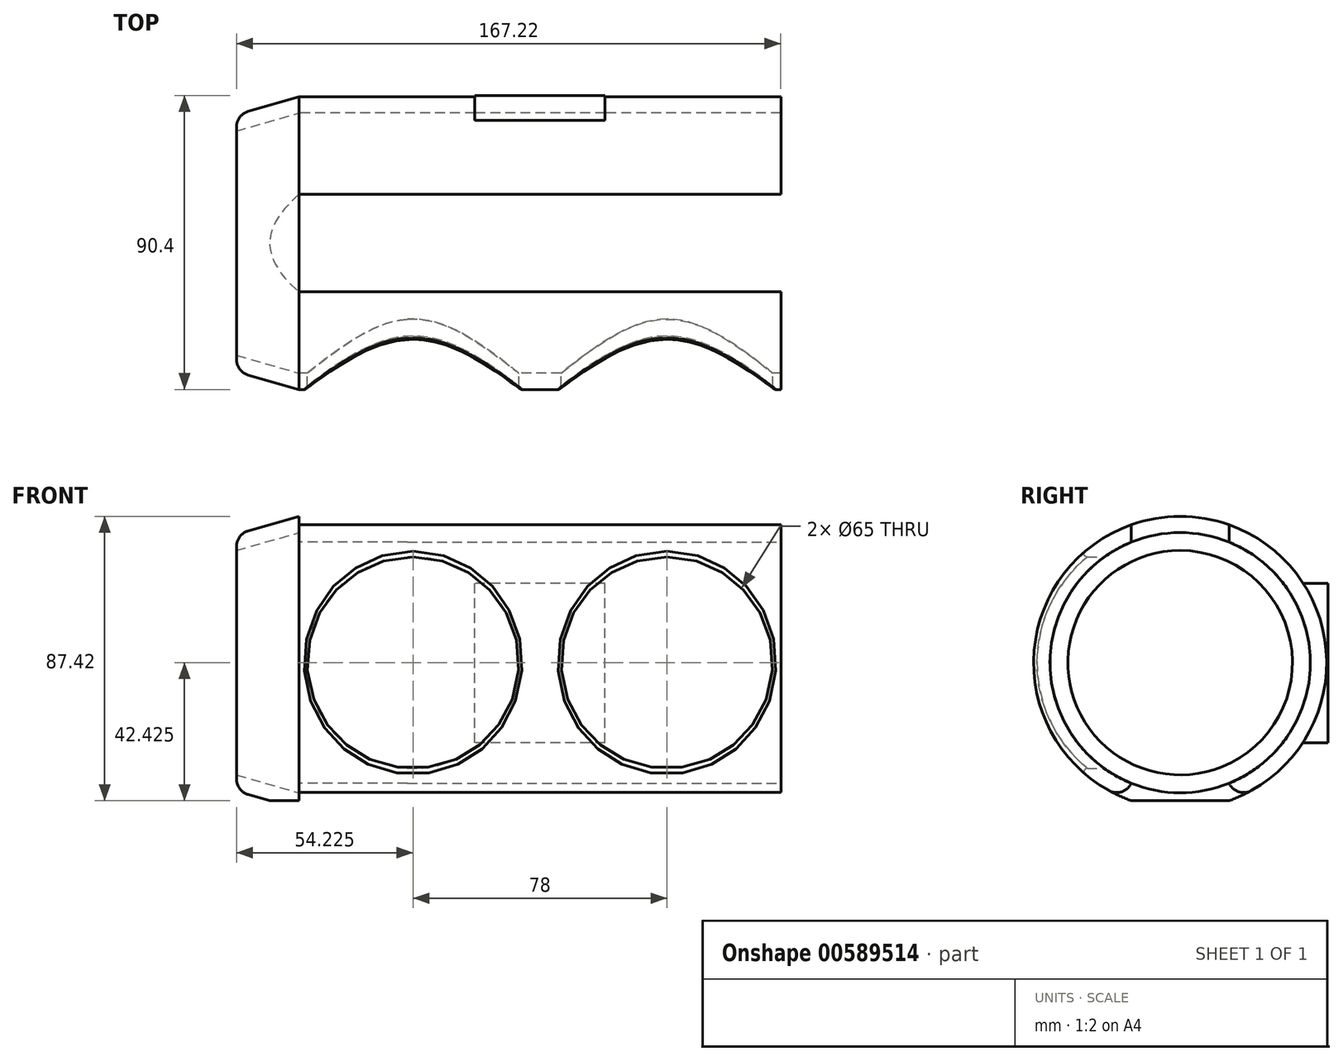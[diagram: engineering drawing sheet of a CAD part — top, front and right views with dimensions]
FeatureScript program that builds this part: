
annotation { "Feature Type Name" : "Feature", "Feature Type Description" : "" }
export const myFeature = defineFeature(function(context is Context, id is Id, definition is map)
    precondition{}
    {
        {
            var Q0;
            Q0=qCreatedBy(makeId("Front.planeOp"),FACE);
            var sketch = newSketch(context, id + "F0", { "sketchPlane" : qUnion([Q0])});
            skLineSegment(sketch, "E0.left", {"start": v(-52.48, 41.98) * mm, "end": v(-52.48, 7.48) * mm});
            skLineSegment(sketch, "E0.right", {"start": v(-33.26, 47.48) * mm, "end": v(-33.26, 7.48) * mm});
            skLineSegment(sketch, "E1", {"start": v(-52.48, 41.98) * mm, "end": v(-33.26, 47.48) * mm});
            skLineSegment(sketch, "E2", {"start": v(-52.48, 7.48) * mm, "end": v(-33.26, 7.48) * mm});
            skLineSegment(sketch, "E3", {"start": v(-33.26, 47.48) * mm, "end": v(-33.26, 52.48) * mm});
            skLineSegment(sketch, "E4", {"start": v(-52.48, 41.98) * mm, "end": v(-52.48, 46.98) * mm});
            skLineSegment(sketch, "E5", {"start": v(-52.48, 46.98) * mm, "end": v(-33.26, 52.48) * mm});
            skLineSegment(sketch, "E6.MirrorCS", {"start": v(-33.26, -32.52) * mm, "end": v(-33.26, 7.48) * mm});
            skLineSegment(sketch, "E7.MirrorCS", {"start": v(-52.48, -27.02) * mm, "end": v(-52.48, 7.48) * mm});
            skLineSegment(sketch, "E8.MirrorCS", {"start": v(-52.48, -27.02) * mm, "end": v(-33.26, -32.52) * mm});
            skLineSegment(sketch, "E9.MirrorCS", {"start": v(-52.48, -32.02) * mm, "end": v(-33.26, -37.52) * mm});
            skLineSegment(sketch, "E10.MirrorCS", {"start": v(-52.48, -27.02) * mm, "end": v(-52.48, -32.02) * mm});
            skLineSegment(sketch, "E11.MirrorCS", {"start": v(-33.26, -32.52) * mm, "end": v(-33.26, -37.52) * mm});
            skLineSegment(sketch, "E12", {"start": v(-33.26, 47.48) * mm, "end": v(114.74, 47.48) * mm});
            skLineSegment(sketch, "E13", {"start": v(40.74, 47.48) * mm, "end": v(40.74, -32.52) * mm});
            skLineSegment(sketch, "E14.MirrorCS", {"start": v(114.74, -32.52) * mm, "end": v(114.74, 7.48) * mm});
            skLineSegment(sketch, "E15.MirrorCS", {"start": v(114.74, 47.48) * mm, "end": v(114.74, 7.48) * mm});
            skLineSegment(sketch, "E16.MirrorCS", {"start": v(114.74, -32.52) * mm, "end": v(114.74, -37.52) * mm});
            skLineSegment(sketch, "E17.MirrorCS", {"start": v(114.74, 47.48) * mm, "end": v(114.74, 52.48) * mm});
            skLineSegment(sketch, "E18.MirrorCS", {"start": v(114.74, 47.48) * mm, "end": v(-33.26, 47.48) * mm});
            skLineSegment(sketch, "E19.MirrorCS", {"start": v(-33.26, -32.52) * mm, "end": v(114.74, -32.52) * mm});
            skLineSegment(sketch, "E20", {"start": v(-33.26, 52.48) * mm, "end": v(114.74, 52.48) * mm});
            skLineSegment(sketch, "E21", {"start": v(-33.26, -37.52) * mm, "end": v(114.74, -37.52) * mm});
            skSolve(sketch);
        }
        {
            var Q0;
            Q0=makeQuery(id+"F0.imprint","IMPRINT",FACE,{"disambiguationData":[TD([[makeQuery(id+"F0.imprint","IMPRINT",EDGE,{"derivedFrom":sQuery(id+"F0.wireOp",EDGE,"E1")}),1.0]])]});
            var Q1;
            Q1=makeQuery(id+"F0.imprint","IMPRINT",FACE,{"disambiguationData":[TD([[makeQuery(id+"F0.imprint","IMPRINT",EDGE,{"derivedFrom":sQuery(id+"F0.wireOp",EDGE,"c2bfdc4a-e5b6-459e-925a-0be5c92ff4e80.MirrorCS")}),-1.0]])]});
            var Q2;
            {var subQ1=sQuery(id+"F0.wireOp",EDGE,"E3");Q2=makeQuery(id+"F0.imprint","IMPRINT",FACE,{"disambiguationData":[TD([[makeQuery(id+"F0.imprint","IMPRINT",EDGE,{"derivedFrom":subQ1}),-1.0]])]});}
            var Q3;
            Q3=sQuery(id+"F0.wireOp",EDGE,"E2");
            revolve(context, id + "F1", {"entities" : qUnion([Q0, Q1, Q2]), "axis" : qUnion([Q3]), "revolveType" : RevolveType.FULL});
        }
        {
            var Q0;
            Q0=qCreatedBy(makeId("Top.planeOp"),FACE);
            var sketch = newSketch(context, id + "F2", { "sketchPlane" : qUnion([Q0])});
            skLineSegment(sketch, "E22", {"start": v(-33.26, 0) * mm, "end": v(114.74, 0) * mm});
            skLineSegment(sketch, "E23.bottom", {"start": v(114.74, -15) * mm, "end": v(-33.26, -15) * mm});
            skLineSegment(sketch, "E23.top", {"start": v(114.74, 15) * mm, "end": v(-33.26, 15) * mm});
            skLineSegment(sketch, "E23.left", {"start": v(114.74, -15) * mm, "end": v(114.74, 15) * mm});
            skLineSegment(sketch, "E23.right", {"start": v(-33.26, -15) * mm, "end": v(-33.26, 15) * mm});
            skPoint(sketch, "E23.middle", {"position": v(40.74, 0) * mm});
            skSolve(sketch);
        }
        {
            var Q0;
            Q0 = qSketchRegion(id + "F2", true);
            extrude(context, id + "F3", {"entities" : qUnion([Q0]), "operationType" : NewBodyOperationType.REMOVE, "endBound" : BoundingType.SYMMETRIC, "depth" : 116.8 * mm, "offsetDistance" : 25 * mm});
        }
        {
            var Q0;
            Q0=qCreatedBy(makeId("Front.planeOp"),FACE);
            var sketch = newSketch(context, id + "F4", { "sketchPlane" : qUnion([Q0])});
            skCircle(sketch, "E24", {"center": v(1.74, 7.48) * mm, "radius": 32.5 * mm});
            skCircle(sketch, "E25", {"center": v(79.74, 7.48) * mm, "radius": 32.5 * mm});
            skSolve(sketch);
        }
        {
            var Q0;
            Q0=qCreatedBy(makeId("Front.planeOp"),FACE);
            var sketch = newSketch(context, id + "F5", { "sketchPlane" : qUnion([Q0])});
            skLineSegment(sketch, "E26.bottom", {"start": v(-49.57, -47.9) * mm, "end": v(133.44, -47.9) * mm});
            skLineSegment(sketch, "E26.top", {"start": v(-49.57, -34.94) * mm, "end": v(133.44, -34.94) * mm});
            skLineSegment(sketch, "E26.left", {"start": v(-49.57, -47.9) * mm, "end": v(-49.57, -34.94) * mm});
            skLineSegment(sketch, "E26.right", {"start": v(133.44, -47.9) * mm, "end": v(133.44, -34.94) * mm});
            skSolve(sketch);
        }
        {
            var Q0;
            Q0 = qSketchRegion(id + "F5", true);
            extrude(context, id + "F6", {"entities" : qUnion([Q0]), "operationType" : NewBodyOperationType.REMOVE, "endBound" : BoundingType.SYMMETRIC, "oppositeDirection" : true, "depth" : 70.2 * mm, "offsetDistance" : 25 * mm});
        }
        {
            var Q0;
            Q0=makeQuery(id+"F1.opRevolve","SWEPT_EDGE",EDGE,{"disambiguationData":[OSD([sQuery(id+"F0.wireOp",EDGE,"a673c032-d0a1-4c3f-9cd5-afd58c44c5de0.MirrorCS"),sQuery(id+"F0.wireOp",EDGE,"f61c0853-5b7b-4805-88cf-b8fb3abf6acf0.MirrorCS")])]});
            var Q1;
            Q1=makeQuery(id+"F3.boolean.opBoolean","INTERSECT",EDGE,{"disambiguationData":[OD(1.0)],"derivedFrom":[makeQuery(id+"F1.opRevolve","SWEPT_FACE",FACE,{"disambiguationData":[OSD([sQuery(id+"F0.wireOp",EDGE,"E20")])]}),makeQuery(id+"F3.opExtrude","SWEPT_FACE",FACE,{"disambiguationData":[OSD([sQuery(id+"F2.wireOp",EDGE,"E23.top")])]})]});
            var Q2;
            Q2=makeQuery(id+"F3.boolean.opBoolean","INTERSECT",EDGE,{"disambiguationData":[OD(1.0)],"derivedFrom":[makeQuery(id+"F1.opRevolve","SWEPT_FACE",FACE,{"disambiguationData":[OSD([sQuery(id+"F0.wireOp",EDGE,"E20")])]}),makeQuery(id+"F3.opExtrude","SWEPT_FACE",FACE,{"disambiguationData":[OSD([sQuery(id+"F2.wireOp",EDGE,"E23.bottom")])]})]});
            var Q3;
            Q3=makeQuery(id+"F1.opRevolve","SWEPT_EDGE",EDGE,{"disambiguationData":[OSD([sQuery(id+"F0.wireOp",EDGE,"E4"),sQuery(id+"F0.wireOp",EDGE,"E5")])]});
            fillet(context, id + "F7", {"entities" : qUnion([Q0, Q1, Q2, Q3]), "radius" : 5 * mm, "tangentPropagation" : true, "allowEdgeOverflow" : false});
        }
        {
            var Q0;
            Q0 = qSketchRegion(id + "F4", true);
            extrude(context, id + "F8", {"entities" : qUnion([Q0]), "operationType" : NewBodyOperationType.REMOVE, "depth" : 115.2 * mm, "offsetDistance" : 25 * mm});
        }
        {
            var Q0;
            Q0 = qSketchRegion(id + "F4", true);
            extrude(context, id + "F9", {"entities" : qUnion([Q0]), "operationType" : NewBodyOperationType.REMOVE, "depth" : 103.5 * mm, "offsetDistance" : 25 * mm});
        }
        {
            var Q0;
            Q0=makeQuery(id+"F8.boolean.opBoolean","INTERSECT",EDGE,{"derivedFrom":[makeQuery(id+"F3.boolean.opBoolean","SPLIT",FACE,{"disambiguationData":[TD([makeQuery(id+"F3.opExtrude","SWEPT_FACE",FACE,{"disambiguationData":[OSD([sQuery(id+"F2.wireOp",EDGE,"E23.bottom")])]})])],"derivedFrom":makeQuery(id+"F1.opRevolve","SWEPT_FACE",FACE,{"disambiguationData":[OSD([sQuery(id+"F0.wireOp",EDGE,"E20")])]})}),makeQuery(id+"F8.opExtrude","SWEPT_FACE",FACE,{"disambiguationData":[OSD([sQuery(id+"F4.wireOp",EDGE,"E24")])]})]});
            var Q1;
            Q1=makeQuery(id+"F8.boolean.opBoolean","INTERSECT",EDGE,{"derivedFrom":[makeQuery(id+"F3.boolean.opBoolean","SPLIT",FACE,{"disambiguationData":[TD([makeQuery(id+"F3.opExtrude","SWEPT_FACE",FACE,{"disambiguationData":[OSD([sQuery(id+"F2.wireOp",EDGE,"E23.bottom")])]})])],"derivedFrom":makeQuery(id+"F1.opRevolve","SWEPT_FACE",FACE,{"disambiguationData":[OSD([sQuery(id+"F0.wireOp",EDGE,"E20")])]})}),makeQuery(id+"F8.opExtrude","SWEPT_FACE",FACE,{"disambiguationData":[OSD([sQuery(id+"F4.wireOp",EDGE,"E25")])]})]});
            fillet(context, id + "F10", {"entities" : qUnion([Q0, Q1]), "radius" : 1 * mm, "tangentPropagation" : true, "allowEdgeOverflow" : false});
        }
        {
            var Q0;
            Q0=qCreatedBy(makeId("Front.planeOp"),FACE);
            var sketch = newSketch(context, id + "F11", { "sketchPlane" : qUnion([Q0])});
            skLineSegment(sketch, "E27.bottom", {"start": v(20.74, -17.13) * mm, "end": v(60.74, -17.13) * mm});
            skLineSegment(sketch, "E27.top", {"start": v(20.74, 31.88) * mm, "end": v(60.74, 31.88) * mm});
            skLineSegment(sketch, "E27.left", {"start": v(20.74, -17.13) * mm, "end": v(20.74, 31.88) * mm});
            skLineSegment(sketch, "E27.right", {"start": v(60.74, -17.13) * mm, "end": v(60.74, 31.88) * mm});
            skPoint(sketch, "E27.middle", {"position": v(40.74, 7.38) * mm});
            skSolve(sketch);
        }
        {
            var Q0;
            Q0 = qSketchRegion(id + "F11", true);
            extrude(context, id + "F12", {"entities" : qUnion([Q0]), "operationType" : NewBodyOperationType.ADD, "oppositeDirection" : true, "depth" : 45.4 * mm, "offsetDistance" : 25 * mm});
        }
        {
            var Q0;
            Q0=qCreatedBy(makeId("Right.planeOp"),FACE);
            var sketch = newSketch(context, id + "F13", { "sketchPlane" : qUnion([Q0])});
            skCircle(sketch, "E28", {"center": v(0, 7.49) * mm, "radius": 40 * mm});
            skSolve(sketch);
        }
        {
            var Q0;
            Q0 = qSketchRegion(id + "F13", true);
            extrude(context, id + "F14", {"entities" : qUnion([Q0]), "operationType" : NewBodyOperationType.REMOVE, "depth" : 160 * mm, "offsetDistance" : 25 * mm});
        }
    });
